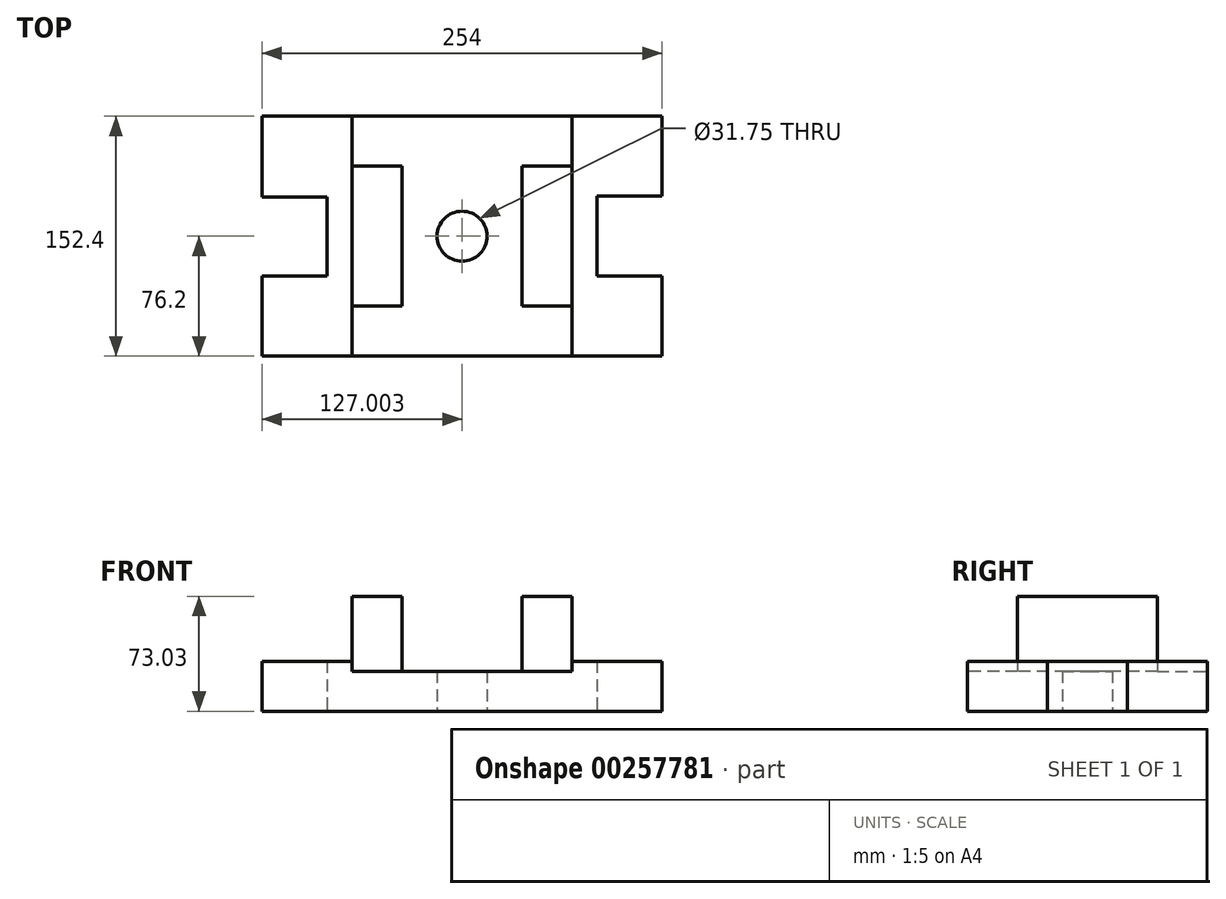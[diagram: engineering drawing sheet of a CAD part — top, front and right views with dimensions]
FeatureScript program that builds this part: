
annotation { "Feature Type Name" : "Feature", "Feature Type Description" : "" }
export const myFeature = defineFeature(function(context is Context, id is Id, definition is map)
    precondition{}
    {
        {
            var Q0;
            Q0=qCreatedBy(makeId("Top.planeOp"),FACE);
            var sketch = newSketch(context, id + "F0", { "sketchPlane" : qUnion([Q0])});
            skLineSegment(sketch, "E0.top", {"start": v(-146.96, -50.8) * mm, "end": v(107.04, -50.8) * mm});
            skLineSegment(sketch, "E0.left", {"start": v(-146.96, 101.6) * mm, "end": v(-146.96, 50.27) * mm});
            skLineSegment(sketch, "E0.right", {"start": v(107.04, 0) * mm, "end": v(107.04, -50.8) * mm});
            skLineSegment(sketch, "E1.top", {"start": v(-146.96, 50.27) * mm, "end": v(-105.68, 50.27) * mm});
            skLineSegment(sketch, "E2.top", {"start": v(-146.96, 0) * mm, "end": v(-105.68, 0) * mm});
            skLineSegment(sketch, "E2.right", {"start": v(-105.68, 50.27) * mm, "end": v(-105.68, 0) * mm});
            skLineSegment(sketch, "E3.trimOffspring", {"start": v(-146.96, 0) * mm, "end": v(-146.96, -50.8) * mm});
            skLineSegment(sketch, "E4.top", {"start": v(107.04, 50.8) * mm, "end": v(65.77, 50.8) * mm});
            skLineSegment(sketch, "E4.left", {"start": v(107.04, 101.6) * mm, "end": v(107.04, 50.8) * mm});
            skLineSegment(sketch, "E5.top", {"start": v(107.04, 0) * mm, "end": v(65.77, 0) * mm});
            skLineSegment(sketch, "E5.right", {"start": v(65.77, 50.8) * mm, "end": v(65.77, 0) * mm});
            skLineSegment(sketch, "E6", {"start": v(49.9, 101.6) * mm, "end": v(18.14, 101.6) * mm});
            skLineSegment(sketch, "E7.trimOffspring", {"start": v(49.9, 101.6) * mm, "end": v(107.04, 101.6) * mm});
            skLineSegment(sketch, "E8", {"start": v(-146.96, 101.6) * mm, "end": v(18.14, 101.6) * mm});
            skLineSegment(sketch, "E9.right", {"start": v(-58.06, 101.6) * mm, "end": v(-58.06, -50.8) * mm});
            skLineSegment(sketch, "E10", {"start": v(-89.8, 69.85) * mm, "end": v(-58.06, 69.85) * mm});
            skLineSegment(sketch, "E11", {"start": v(-89.8, -50.8) * mm, "end": v(-89.8, 101.6) * mm});
            skLineSegment(sketch, "E12", {"start": v(-89.8, -19.05) * mm, "end": v(-58.06, -19.05) * mm});
            skLineSegment(sketch, "E13", {"start": v(18.14, 101.6) * mm, "end": v(18.14, -50.8) * mm});
            skLineSegment(sketch, "E14", {"start": v(18.14, 69.85) * mm, "end": v(49.9, 69.85) * mm});
            skLineSegment(sketch, "E15", {"start": v(49.9, -19.05) * mm, "end": v(18.14, -19.05) * mm});
            skCircle(sketch, "E16", {"center": v(-19.96, 25.4) * mm, "radius": 15.88 * mm});
            skLineSegment(sketch, "E17", {"start": v(49.9, 101.6) * mm, "end": v(49.9, -50.8) * mm});
            skSolve(sketch);
        }
        {
            var Q0;
            Q0 = qSketchRegion(id + "F0", true);
            extrude(context, id + "F1", {"entities" : qUnion([Q0]), "depth" : 25.4 * mm});
        }
        {
            var Q0;
            {var subQ5=sQuery(id+"F0.wireOp",EDGE,"E0.left");Q0=makeQuery(id+"F0.imprint","IMPRINT",FACE,{"disambiguationData":[TD([[makeQuery(id+"F0.imprint","IMPRINT",EDGE,{"derivedFrom":subQ5}),1.0]])]});}
            var Q1;
            {var subQ7=sQuery(id+"F0.wireOp",EDGE,"E0.right");Q1=makeQuery(id+"F0.imprint","IMPRINT",FACE,{"disambiguationData":[TD([[makeQuery(id+"F0.imprint","IMPRINT",EDGE,{"derivedFrom":subQ7}),-1.0]])]});}
            extrude(context, id + "F2", {"entities" : qUnion([Q0, Q1]), "operationType" : NewBodyOperationType.ADD, "depth" : 31.75 * mm});
        }
        {
            var Q0;
            Q0=makeQuery(id+"F0.imprint","IMPRINT",FACE,{"disambiguationData":[TD([[makeQuery(id+"F0.imprint","IMPRINT",EDGE,{"derivedFrom":sQuery(id+"F0.wireOp",EDGE,"E16")}),-1.0]])]});
            extrude(context, id + "F3", {"entities" : qUnion([Q0]), "operationType" : NewBodyOperationType.ADD, "depth" : 17 / 203.2 * mm});
        }
        {
            var Q0;
            {var subQ0=sQuery(id+"F0.wireOp",EDGE,"E10");Q0=makeQuery(id+"F0.imprint","IMPRINT",FACE,{"disambiguationData":[TD([[makeQuery(id+"F0.imprint","IMPRINT",EDGE,{"derivedFrom":subQ0}),-1.0]])]});}
            var Q1;
            {var subQ0=sQuery(id+"F0.wireOp",EDGE,"E14");Q1=makeQuery(id+"F0.imprint","IMPRINT",FACE,{"disambiguationData":[TD([[makeQuery(id+"F0.imprint","IMPRINT",EDGE,{"derivedFrom":subQ0}),-1.0]])]});}
            extrude(context, id + "F4", {"entities" : qUnion([Q0, Q1]), "operationType" : NewBodyOperationType.ADD, "depth" : 73.02 * mm});
        }
        {
            var Q0;
            {var subQ5=sQuery(id+"F0.wireOp",EDGE,"E10");Q0=makeQuery(id+"F0.imprint","IMPRINT",FACE,{"disambiguationData":[TD([[makeQuery(id+"F0.imprint","IMPRINT",EDGE,{"derivedFrom":subQ5}),1.0]])]});}
            var Q1;
            {var subQ0=sQuery(id+"F0.wireOp",EDGE,"E6");Q1=makeQuery(id+"F0.imprint","IMPRINT",FACE,{"disambiguationData":[TD([[makeQuery(id+"F0.imprint","IMPRINT",EDGE,{"derivedFrom":subQ0}),1.0]])]});}
            var Q2;
            {var subQ5=sQuery(id+"F0.wireOp",EDGE,"E15");Q2=makeQuery(id+"F0.imprint","IMPRINT",FACE,{"disambiguationData":[TD([[makeQuery(id+"F0.imprint","IMPRINT",EDGE,{"derivedFrom":subQ5}),1.0]])]});}
            var Q3;
            {var subQ5=sQuery(id+"F0.wireOp",EDGE,"E12");Q3=makeQuery(id+"F0.imprint","IMPRINT",FACE,{"disambiguationData":[TD([[makeQuery(id+"F0.imprint","IMPRINT",EDGE,{"derivedFrom":subQ5}),-1.0]])]});}
            extrude(context, id + "F5", {"entities" : qUnion([Q0, Q1, Q2, Q3]), "operationType" : NewBodyOperationType.ADD, "depth" : 29 / 203.2 * mm});
        }
    });
